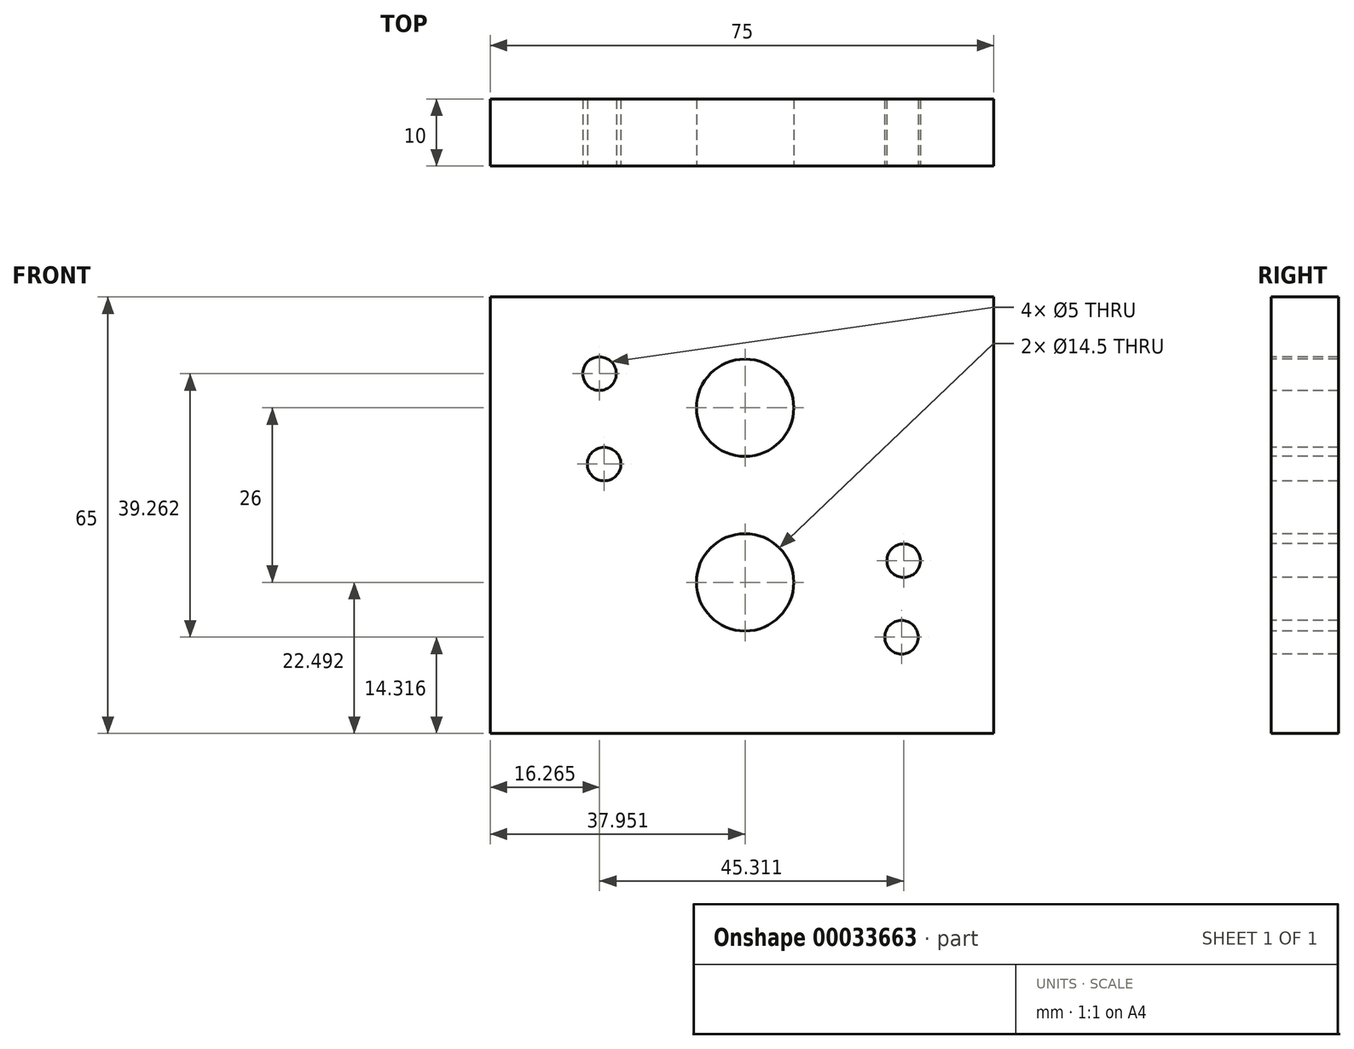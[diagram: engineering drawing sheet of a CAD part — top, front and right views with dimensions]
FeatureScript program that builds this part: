
annotation { "Feature Type Name" : "Feature", "Feature Type Description" : "" }
export const myFeature = defineFeature(function(context is Context, id is Id, definition is map)
    precondition{}
    {
        {
            var Q0;
            Q0=qCreatedBy(makeId("Front.planeOp"),FACE);
            var sketch = newSketch(context, id + "F0", { "sketchPlane" : qUnion([Q0])});
            skLineSegment(sketch, "E0.bottom", {"start": v(0, 0) * mm, "end": v(75, 0) * mm});
            skLineSegment(sketch, "E0.top", {"start": v(0, 65) * mm, "end": v(75, 65) * mm});
            skLineSegment(sketch, "E0.left", {"start": v(0, 0) * mm, "end": v(0, 65) * mm});
            skLineSegment(sketch, "E0.right", {"start": v(75, 0) * mm, "end": v(75, 65) * mm});
            skSolve(sketch);
        }
        {
            var Q0;
            Q0 = qSketchRegion(id + "F0", true);
            extrude(context, id + "F1", {"entities" : qUnion([Q0]), "depth" : 10 * mm});
        }
        {
            var Q0;
            Q0=makeQuery(id+"F1.opExtrude","CAP_FACE",FACE,{"disambiguationData":[OSD([sQuery(id+"F0.wireOp",EDGE,"E0.bottom"),sQuery(id+"F0.wireOp",EDGE,"E0.top"),sQuery(id+"F0.wireOp",EDGE,"E0.left"),sQuery(id+"F0.wireOp",EDGE,"E0.right")])],"isStart":false});
            var sketch = newSketch(context, id + "F2", { "sketchPlane" : qUnion([Q0])});
            skCircle(sketch, "E1", {"center": v(37.95, 48.5) * mm, "radius": 7.25 * mm});
            skCircle(sketch, "E2", {"center": v(37.95, 22.5) * mm, "radius": 7.25 * mm});
            skSolve(sketch);
        }
        {
            var Q0;
            Q0=sQuery(id+"F2.wireOp",VERTEX,"E1.center");
            var Q1;
            Q1=sQuery(id+"F2.wireOp",VERTEX,"E2.center");
            var Q2;
            Q2=makeQuery(id+"F1.opExtrude","SWEPT_BODY",BODY,{"disambiguationData":[OSD([sQuery(id+"F0.wireOp",EDGE,"E0.bottom"),sQuery(id+"F0.wireOp",EDGE,"E0.top"),sQuery(id+"F0.wireOp",EDGE,"E0.left"),sQuery(id+"F0.wireOp",EDGE,"E0.right")])]});
            hole(context, id + "F3", {"style" : HoleStyle.SIMPLE, "holeDiameter" : 14.5 * mm, "endStyle" : HoleEndStyle.THROUGH, "locations" : qUnion([Q0, Q1]), "scope" : qUnion([Q2])});
        }
        {
            var Q0;
            Q0=makeQuery(id+"F1.opExtrude","CAP_FACE",FACE,{"disambiguationData":[OSD([sQuery(id+"F0.wireOp",EDGE,"E0.bottom"),sQuery(id+"F0.wireOp",EDGE,"E0.top"),sQuery(id+"F0.wireOp",EDGE,"E0.left"),sQuery(id+"F0.wireOp",EDGE,"E0.right")])],"isStart":false});
            var sketch = newSketch(context, id + "F4", { "sketchPlane" : qUnion([Q0])});
            skPoint(sketch, "E3", {"position": v(16.27, 53.58) * mm});
            skPoint(sketch, "E4", {"position": v(16.95, 40.1) * mm});
            skPoint(sketch, "E5", {"position": v(61.58, 25.72) * mm});
            skPoint(sketch, "E6", {"position": v(61.26, 14.32) * mm});
            skSolve(sketch);
        }
        {
            var Q0;
            Q0=sQuery(id+"F4.wireOp",VERTEX,"E3");
            var Q1;
            Q1=sQuery(id+"F4.wireOp",VERTEX,"E4");
            var Q2;
            Q2=sQuery(id+"F4.wireOp",VERTEX,"E5");
            var Q3;
            Q3=sQuery(id+"F4.wireOp",VERTEX,"E6");
            var Q4;
            Q4=makeQuery(id+"F1.opExtrude","SWEPT_BODY",BODY,{"disambiguationData":[OSD([sQuery(id+"F0.wireOp",EDGE,"E0.bottom"),sQuery(id+"F0.wireOp",EDGE,"E0.top"),sQuery(id+"F0.wireOp",EDGE,"E0.left"),sQuery(id+"F0.wireOp",EDGE,"E0.right")])]});
            hole(context, id + "F5", {"style" : HoleStyle.SIMPLE, "holeDiameter" : 5 * mm, "endStyle" : HoleEndStyle.THROUGH, "locations" : qUnion([Q0, Q1, Q2, Q3]), "scope" : qUnion([Q4])});
        }
    });
